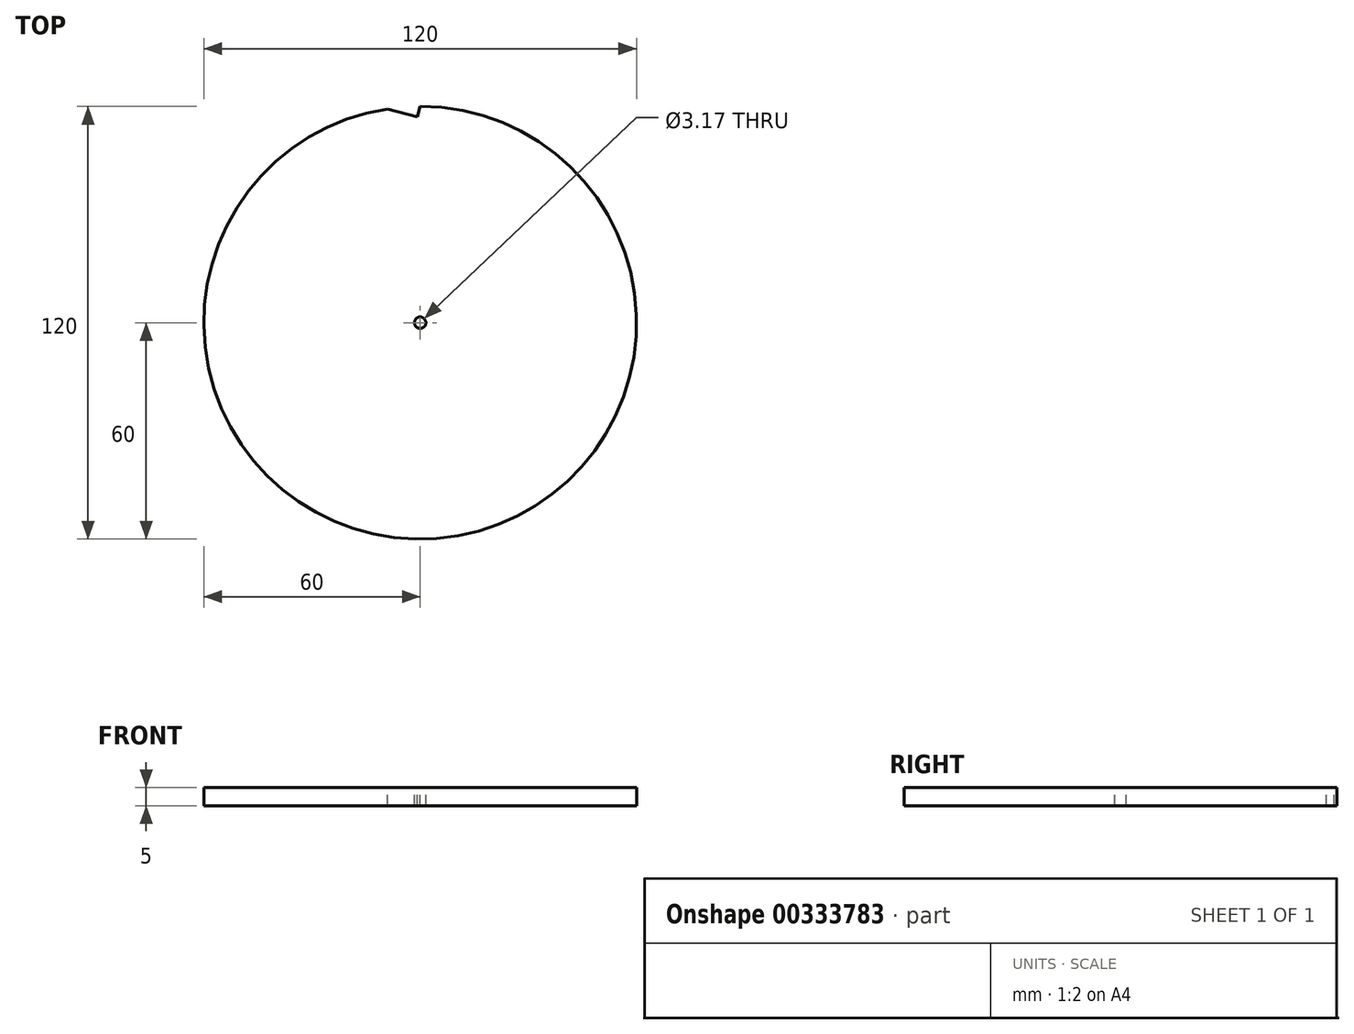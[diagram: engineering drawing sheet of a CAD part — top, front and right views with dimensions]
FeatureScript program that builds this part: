
annotation { "Feature Type Name" : "Feature", "Feature Type Description" : "" }
export const myFeature = defineFeature(function(context is Context, id is Id, definition is map)
    precondition{}
    {
        {
            assignVariable(context, id + "F0", {"name" : "faceWidth", "anyValue" : 5});
        }
        {
            var Q0;
            Q0=qCreatedBy(makeId("Top.planeOp"),FACE);
            var sketch = newSketch(context, id + "F1", { "sketchPlane" : qUnion([Q0])});
            skCircle(sketch, "E0", {"center": v(0, 0) * mm, "radius": 60 * mm});
            skSolve(sketch);
        }
        {
            var Q0;
            Q0=qSketchRegion(id+"F1",true);
            extrude(context, id + "F2", {"entities" : qUnion([Q0]), "depth" : (getVariable(context, 'faceWidth')) * mm});
        }
        {
            var Q0;
            Q0=makeQuery(id+"F2.opExtrude","CAP_FACE",FACE,{"disambiguationData":[OSD([sQuery(id+"F1.wireOp",EDGE,"E0")])],"isStart":false});
            var sketch = newSketch(context, id + "F3", { "sketchPlane" : qUnion([Q0])});
            skLineSegment(sketch, "E1", {"start": v(0, 60) * mm, "end": v(-0.78, 57.1) * mm});
            skLineSegment(sketch, "E2", {"start": v(-0.78, 57.1) * mm, "end": v(-9.04, 59.32) * mm});
            skSolve(sketch);
        }
        {
            var Q0;
            Q0=qSketchRegion(id+"F3",true);
            var Q1;
            {var subQ0=sQuery(id+"F3.wireOp",EDGE,"E1");Q1=makeQuery(id+"F3.imprint","IMPRINT",FACE,{"disambiguationData":[TD([[makeQuery(id+"F3.imprint","IMPRINT",EDGE,{"derivedFrom":subQ0}),-1.0]])]});}
            extrude(context, id + "F4", {"entities" : qUnion([Q0, Q1]), "operationType" : NewBodyOperationType.REMOVE, "endBound" : BoundingType.THROUGH_ALL, "oppositeDirection" : true, "depth" : 25 * mm});
        }
        {
            var Q0;
            Q0=makeQuery(id+"F2.opExtrude","CAP_FACE",FACE,{"disambiguationData":[OSD([sQuery(id+"F1.wireOp",EDGE,"E0")])],"isStart":false});
            var sketch = newSketch(context, id + "F5", { "sketchPlane" : qUnion([Q0])});
            skCircle(sketch, "E3", {"center": v(0, 0) * mm, "radius": 1.59 * mm});
            skSolve(sketch);
        }
        {
            var Q0;
            Q0 = qSketchRegion(id + "F5", true);
            extrude(context, id + "F6", {"entities" : qUnion([Q0]), "operationType" : NewBodyOperationType.REMOVE, "endBound" : BoundingType.THROUGH_ALL, "oppositeDirection" : true, "depth" : 25 * mm});
        }
    });
